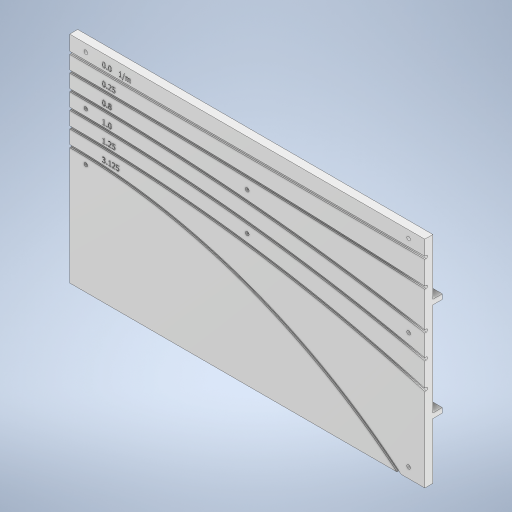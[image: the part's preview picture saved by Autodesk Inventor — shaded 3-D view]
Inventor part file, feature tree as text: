
AUTODESK INVENTOR PART (.ipt)
format: ipt  version: 2023 (Build 270158000, 158)  size: 1,089,024 bytes
history: native  units: mm
features: sketch x14, sweep x6, extrude x3, other x1
ambient origin geometry x8: Origin, YZ Plane, XZ Plane, XY Plane, X Axis, Y Axis, Z Axis, Center Point
bodies: Solide1 (feature_tree)
feature tree (24):
  extrude  "Extrusion1"  Depth=133.5mm
  extrude  "Extrusion2"  Depth=220.0mm
  sweep  "Balayage1"
  sweep  "Balayage2"
  sweep  "Balayage3"
  sweep  "Balayage4"
  sweep  "Balayage5"
  sweep  "Balayage6"
  extrude  "Extrusion3"  Depth=0.85mm
  other  "Gravure1"
  sketch  "Esquisse1"
  sketch  "Esquisse4"
  sketch  "Esquisse5"
  sketch  "Esquisse6"
  sketch  "Esquisse7"
  sketch  "Esquisse8"
  sketch  "Esquisse9"
  sketch  "Esquisse10"
  sketch  "Esquisse11"
  sketch  "Esquisse12"
  sketch  "Esquisse13"
  sketch  "Esquisse14"
  sketch  "Esquisse15"
  sketch  "Esquisse16"
